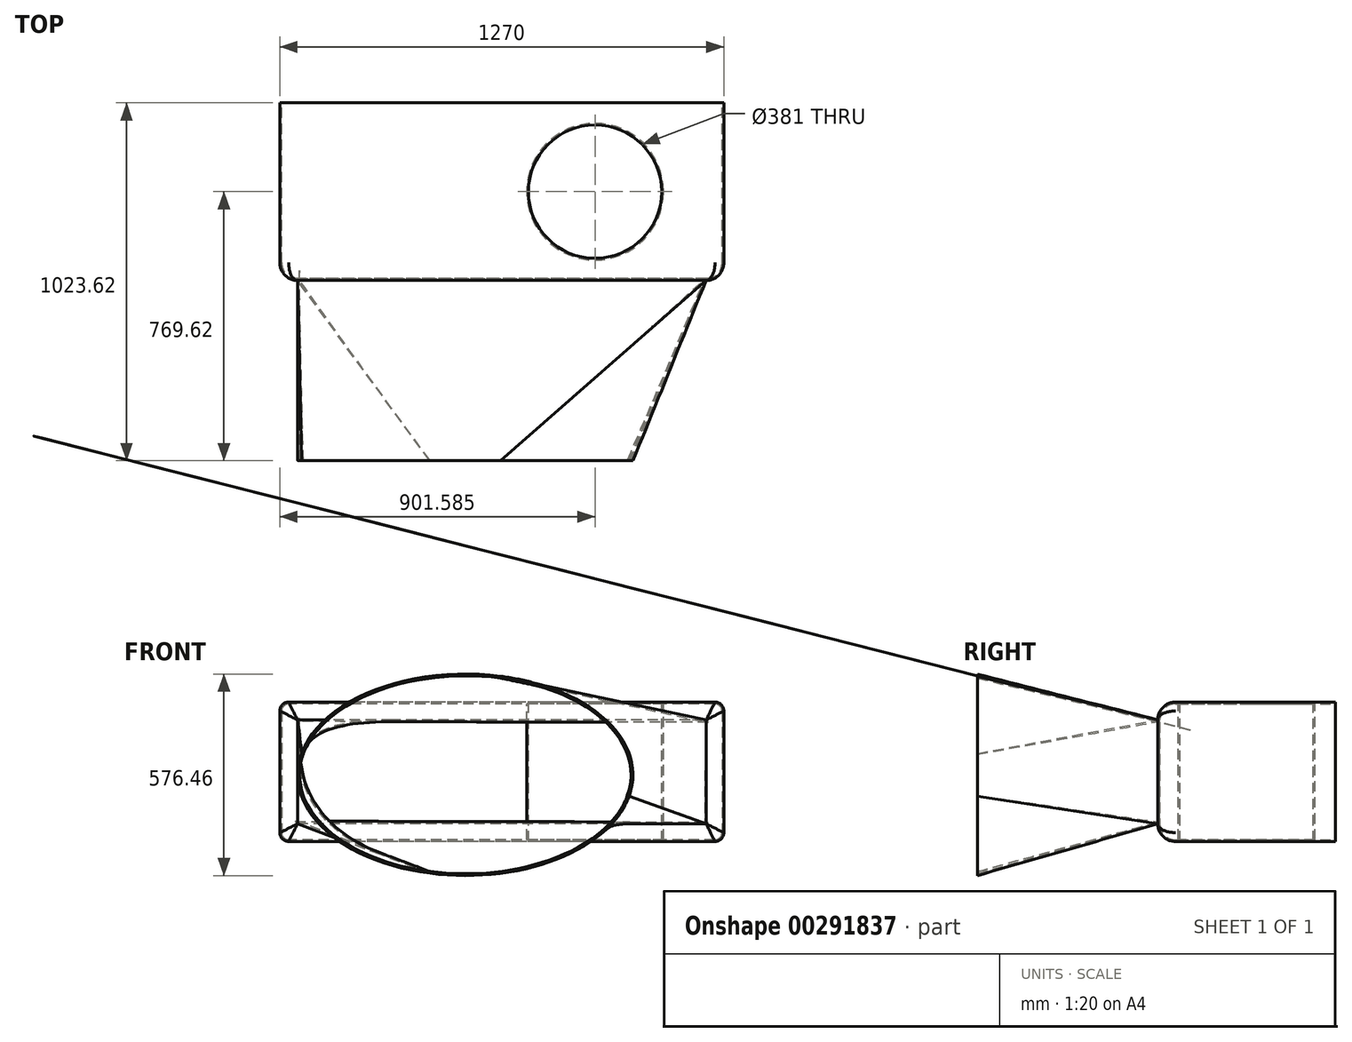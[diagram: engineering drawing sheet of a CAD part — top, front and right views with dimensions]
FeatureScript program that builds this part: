
annotation { "Feature Type Name" : "Feature", "Feature Type Description" : "" }
export const myFeature = defineFeature(function(context is Context, id is Id, definition is map)
    precondition{}
    {
        {
            var Q0;
            Q0=qCreatedBy(makeId("Top.planeOp"),FACE);
            var sketch = newSketch(context, id + "F0", { "sketchPlane" : qUnion([Q0])});
            skLineSegment(sketch, "E0.bottom", {"start": v(635, 254) * mm, "end": v(-635, 254) * mm});
            skLineSegment(sketch, "E0.top", {"start": v(635, -254) * mm, "end": v(-635, -254) * mm});
            skLineSegment(sketch, "E0.left", {"start": v(635, 254) * mm, "end": v(635, -254) * mm});
            skLineSegment(sketch, "E0.right", {"start": v(-635, 254) * mm, "end": v(-635, -254) * mm});
            skPoint(sketch, "E0.middle", {"position": v(0, 0) * mm});
            skSolve(sketch);
        }
        {
            var Q0;
            Q0 = qSketchRegion(id + "F0", true);
            extrude(context, id + "F1", {"entities" : qUnion([Q0]), "depth" : 398.78 * mm});
        }
        {
            var Q0;
            Q0=makeQuery(id+"F1.opExtrude","CAP_EDGE",EDGE,{"disambiguationData":[OSD([sQuery(id+"F0.wireOp",EDGE,"E0.right")])],"isStart":true});
            var Q1;
            Q1=makeQuery(id+"F1.opExtrude","CAP_EDGE",EDGE,{"disambiguationData":[OSD([sQuery(id+"F0.wireOp",EDGE,"E0.left")])],"isStart":true});
            var Q2;
            Q2=makeQuery(id+"F1.opExtrude","CAP_EDGE",EDGE,{"disambiguationData":[OSD([sQuery(id+"F0.wireOp",EDGE,"E0.left")])],"isStart":false});
            var Q3;
            Q3=makeQuery(id+"F1.opExtrude","CAP_EDGE",EDGE,{"disambiguationData":[OSD([sQuery(id+"F0.wireOp",EDGE,"E0.right")])],"isStart":false});
            fillet(context, id + "F2", {"entities" : qUnion([Q0, Q1, Q2, Q3]), "radius" : 25.4 * mm, "tangentPropagation" : true, "allowEdgeOverflow" : false});
        }
        {
            var Q0;
            Q0=makeQuery(id+"F1.opExtrude","SWEPT_EDGE",EDGE,{"disambiguationData":[OSD([sQuery(id+"F0.wireOp",EDGE,"E0.top"),sQuery(id+"F0.wireOp",EDGE,"E0.right")])]});
            var Q1;
            Q1=makeQuery(id+"F1.opExtrude","SWEPT_EDGE",EDGE,{"disambiguationData":[OSD([sQuery(id+"F0.wireOp",EDGE,"E0.top"),sQuery(id+"F0.wireOp",EDGE,"E0.left")])]});
            fillet(context, id + "F3", {"entities" : qUnion([Q0, Q1]), "radius" : 50.8 * mm, "tangentPropagation" : true, "allowEdgeOverflow" : false});
        }
        {
            var Q0;
            Q0=makeQuery(id+"F1.opExtrude","CAP_FACE",FACE,{"disambiguationData":[OSD([sQuery(id+"F0.wireOp",EDGE,"E0.bottom"),sQuery(id+"F0.wireOp",EDGE,"E0.top"),sQuery(id+"F0.wireOp",EDGE,"E0.left"),sQuery(id+"F0.wireOp",EDGE,"E0.right")])],"isStart":false});
            var sketch = newSketch(context, id + "F4", { "sketchPlane" : qUnion([Q0])});
            skPoint(sketch, "E1", {"position": v(266.59, 0) * mm});
            skSolve(sketch);
        }
        {
            var Q0;
            Q0=sQuery(id+"F4.wireOp",VERTEX,"E1");
            var Q1;
            Q1=makeQuery(id+"F1.opExtrude","SWEPT_BODY",BODY,{"disambiguationData":[OSD([sQuery(id+"F0.wireOp",EDGE,"E0.bottom"),sQuery(id+"F0.wireOp",EDGE,"E0.top"),sQuery(id+"F0.wireOp",EDGE,"E0.left"),sQuery(id+"F0.wireOp",EDGE,"E0.right")])]});
            hole(context, id + "F5", {"style" : HoleStyle.SIMPLE, "endStyle" : HoleEndStyle.THROUGH, "holeDiameter" : 381 * mm, "tappedDepth" : 12.7 * mm, "tapClearance" : 3, "locations" : qUnion([Q0]), "scope" : qUnion([Q1])});
        }
        {
            var Q0;
            Q0=makeQuery(id+"F1.opExtrude","SWEPT_FACE",FACE,{"disambiguationData":[OSD([sQuery(id+"F0.wireOp",EDGE,"E0.top")])]});
            cPlane(context, id + "F6", {"entities" : qUnion([Q0]), "cplaneType" : CPlaneType.OFFSET, "offset" : 515.62 * mm, "width" : 152.4 * mm, "height" : 152.4 * mm});
        }
        {
            var Q0;
            Q0=qCreatedBy(id+"F6.planeOp",FACE);
            var sketch = newSketch(context, id + "F7", { "sketchPlane" : qUnion([Q0])});
            skEllipse(sketch, "E2", {"center": v(-104.33, 190.8) * mm, "majorRadius": 479.26 * mm, "minorRadius": 288.23 * mm, "majorAxis": v(1, 0)});
            skSolve(sketch);
        }
        {
            var Q1;
            Q1=makeQuery(id+"F7.imprint","IMPRINT",FACE,{"disambiguationData":[TD([[makeQuery(id+"F7.imprint","IMPRINT",EDGE,{"derivedFrom":sQuery(id+"F7.wireOp",EDGE,"E2")}),1.0]])]});
            var Q2;
            Q2=makeQuery(id+"F1.opExtrude","SWEPT_FACE",FACE,{"disambiguationData":[OSD([sQuery(id+"F0.wireOp",EDGE,"E0.top")])]});
            loft(context, id + "F8", {"operationType" : NewBodyOperationType.ADD, "sheetProfilesArray" : [{ "sheetProfileEntities" : qUnion([Q1]) }, { "sheetProfileEntities" : qUnion([Q2]) }]});
        }
        {
            var Q0;
            Q0=makeQuery(id+"F1.opExtrude","SWEPT_FACE",FACE,{"disambiguationData":[OSD([sQuery(id+"F0.wireOp",EDGE,"E0.bottom")])]});
            var Q1;
            Q1=makeQuery(id+"F8.opLoft","CAP_FACE",FACE,{"disambiguationData":[OSD([makeQuery(id+"F7.imprint","IMPRINT",FACE,{"disambiguationData":[TD([[makeQuery(id+"F7.imprint","IMPRINT",EDGE,{"derivedFrom":sQuery(id+"F7.wireOp",EDGE,"E2")}),1.0]])]})])],"isStart":true});
            shell(context, id + "F9", {"entities" : qUnion([Q0, Q1]), "thickness" : 5.08 * mm});
        }
    });
